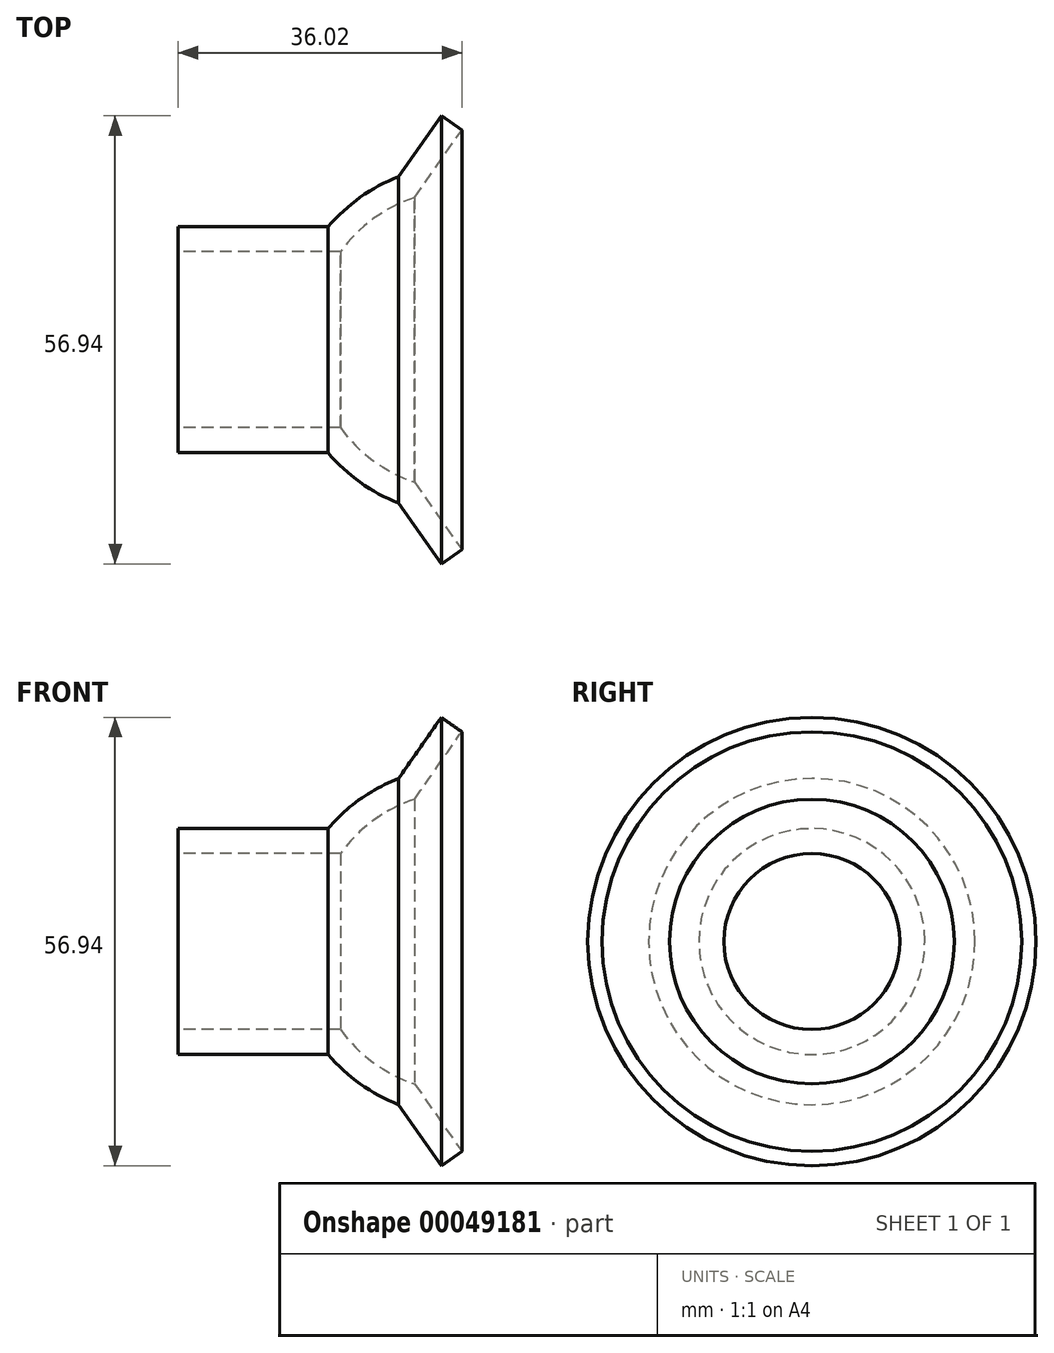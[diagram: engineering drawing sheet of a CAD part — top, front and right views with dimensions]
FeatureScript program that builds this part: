
annotation { "Feature Type Name" : "Feature", "Feature Type Description" : "" }
export const myFeature = defineFeature(function(context is Context, id is Id, definition is map)
    precondition{}
    {
        {
            var Q0;
            Q0=qCreatedBy(makeId("Front.planeOp"),FACE);
            var sketch = newSketch(context, id + "F0", { "sketchPlane" : qUnion([Q0])});
            skLineSegment(sketch, "E0", {"start": v(-65.02, 0) * mm, "end": v(-7.52, 0) * mm, "construction": true});
            skLineSegment(sketch, "E1", {"start": v(-36.02, 14.35) * mm, "end": v(-16.97, 14.35) * mm});
            skLineSegment(sketch, "E2.1", {"start": v(-36.02, 11.18) * mm, "end": v(-15.43, 11.18) * mm});
            skLineSegment(sketch, "E3", {"start": v(-36.02, 14.35) * mm, "end": v(-36.02, 11.18) * mm});
            skArc(sketch, "E4", {"start": v(0, 19.05) * mm, "mid": v(-8.66, 16.97) * mm, "end": v(-15.43, 11.18) * mm});
            skArc(sketch, "E5.0", {"start": v(-8.03, 20.73) * mm, "mid": v(-12.9, 18.1) * mm, "end": v(-16.97, 14.35) * mm});
            skPoint(sketch, "E6", {"position": v(0, 19.05) * mm});
            skLineSegment(sketch, "E7", {"start": v(-6, 18.08) * mm, "end": v(0, 26.65) * mm});
            skLineSegment(sketch, "E8", {"start": v(0, 26.65) * mm, "end": v(-2.6, 28.47) * mm});
            skLineSegment(sketch, "E9", {"start": v(-2.6, 28.47) * mm, "end": v(-8.03, 20.73) * mm});
            skSolve(sketch);
        }
        {
            var Q0;
            Q0 = qSketchRegion(id + "F0", true);
            var Q1;
            Q1=sQuery(id+"F0.wireOp",EDGE,"E0");
            revolve(context, id + "F1", {"entities" : qUnion([Q0]), "axis" : qUnion([Q1]), "revolveType" : RevolveType.FULL});
        }
    });
